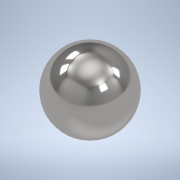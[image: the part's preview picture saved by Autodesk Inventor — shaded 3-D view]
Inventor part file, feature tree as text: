
AUTODESK INVENTOR PART (.ipt)
format: ipt  version: 2021 (Build 250183000, 183)  size: 122,880 bytes
history: native  units: mm
features: revolve x1, sketch x1
ambient origin geometry x8: Origin, YZ Plane, XZ Plane, XY Plane, X Axis, Y Axis, Z Axis, Center Point
bodies: Solid1 (feature_tree)
feature tree (2):
  revolve  "Revolution1"  Angle=90.0deg
  sketch  "Sketch1"  dims[d0=9.5mm d1=90.0deg]
